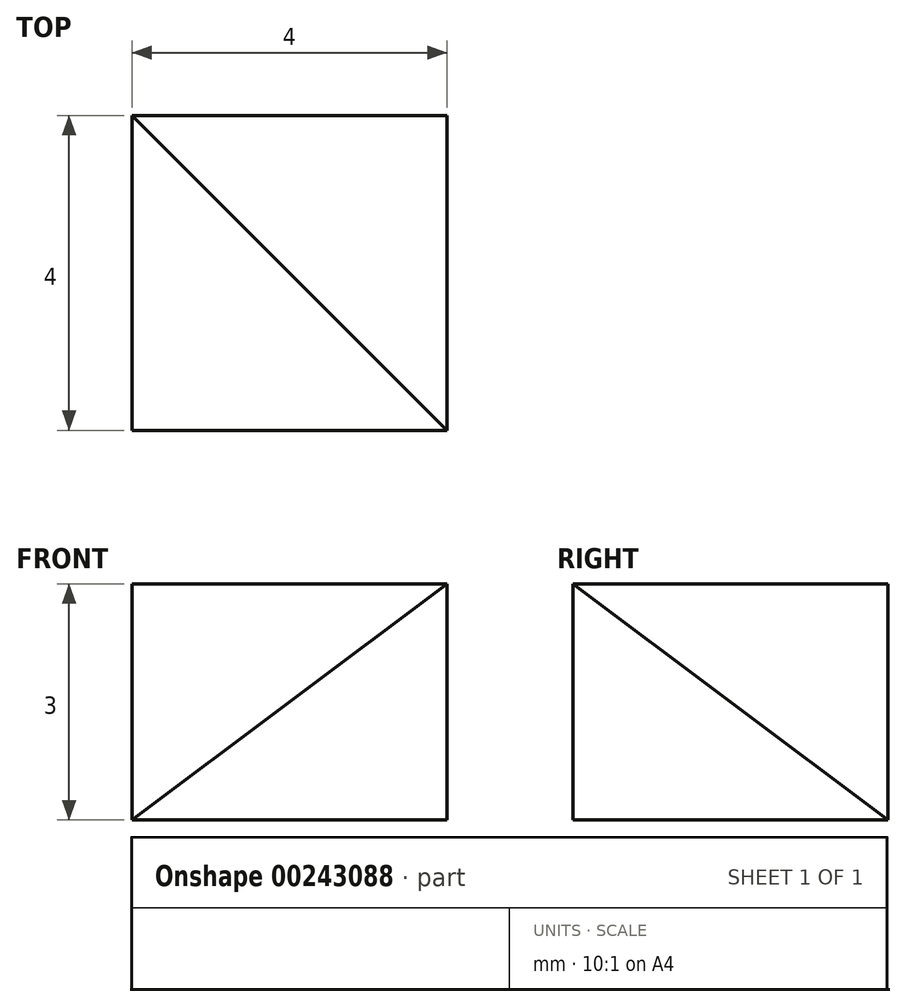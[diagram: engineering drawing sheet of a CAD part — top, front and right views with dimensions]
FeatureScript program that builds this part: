
annotation { "Feature Type Name" : "Feature", "Feature Type Description" : "" }
export const myFeature = defineFeature(function(context is Context, id is Id, definition is map)
    precondition{}
    {
        {
            var Q0;
            Q0=qCreatedBy(makeId("Top.planeOp"),FACE);
            var sketch = newSketch(context, id + "F0", { "sketchPlane" : qUnion([Q0])});
            skLineSegment(sketch, "E0.bottom", {"start": v(0, 0) * mm, "end": v(4, 0) * mm});
            skLineSegment(sketch, "E0.top", {"start": v(0, 4) * mm, "end": v(4, 4) * mm});
            skLineSegment(sketch, "E0.left", {"start": v(0, 0) * mm, "end": v(0, 4) * mm});
            skLineSegment(sketch, "E0.right", {"start": v(4, 0) * mm, "end": v(4, 4) * mm});
            skSolve(sketch);
        }
        {
            var Q0;
            Q0 = qSketchRegion(id + "F0", true);
            extrude(context, id + "F1", {"entities" : qUnion([Q0]), "depth" : 3 * mm});
        }
        {
            var Q0;
            Q0=makeQuery(id+"F1.opExtrude","CAP_VERTEX",VERTEX,{"disambiguationData":[OSD([sQuery(id+"F0.wireOp",EDGE,"E0.top"),sQuery(id+"F0.wireOp",EDGE,"E0.left")])],"isStart":false});
            var Q1;
            Q1=makeQuery(id+"F1.opExtrude","CAP_VERTEX",VERTEX,{"disambiguationData":[OSD([sQuery(id+"F0.wireOp",EDGE,"E0.bottom"),sQuery(id+"F0.wireOp",EDGE,"E0.right")])],"isStart":false});
            var Q2;
            Q2=qCreatedBy(makeId("Origin.pointOp"),VERTEX);
            cPlane(context, id + "F2", {"entities" : qUnion([Q0, Q1, Q2]), "cplaneType" : CPlaneType.THREE_POINT, "offset" : 25 * mm, "width" : 150 * mm, "height" : 150 * mm});
        }
        {
            var Q0;
            Q0=qCreatedBy(id+"F2.planeOp",FACE);
            var sketch = newSketch(context, id + "F3", { "sketchPlane" : qUnion([Q0])});
            skPoint(sketch, "E1.0", {"position": v(0, 5) * mm});
            skPoint(sketch, "E1.1", {"position": v(0, 0) * mm});
            skPoint(sketch, "E1.2", {"position": v(4.66, 1.8) * mm});
            skLineSegment(sketch, "E2", {"start": v(0, 5) * mm, "end": v(4.66, 1.8) * mm});
            skLineSegment(sketch, "E3", {"start": v(0, 0) * mm, "end": v(0, 5) * mm});
            skLineSegment(sketch, "E4", {"start": v(4.66, 1.8) * mm, "end": v(0, 0) * mm});
            skSolve(sketch);
        }
        {
            var Q0;
            Q0 = qSketchRegion(id + "F3", true);
            extrude(context, id + "F4", {"entities" : qUnion([Q0]), "operationType" : NewBodyOperationType.REMOVE, "depth" : 25 * mm});
        }
        {
            var Q0;
            Q0=makeQuery(id+"F4.boolean.opBoolean","MERGE",VERTEX,{"derivedFrom":[makeQuery(id+"F1.opExtrude","CAP_VERTEX",VERTEX,{"disambiguationData":[OSD([sQuery(id+"F0.wireOp",EDGE,"E0.top"),sQuery(id+"F0.wireOp",EDGE,"E0.left")])],"isStart":false}),makeQuery(id+"F4.opExtrude","CAP_VERTEX",VERTEX,{"disambiguationData":[OSD([sQuery(id+"F3.wireOp",EDGE,"E2"),sQuery(id+"F3.wireOp",EDGE,"E3")])],"isStart":true})]});
            var Q1;
            Q1=makeQuery(id+"F4.boolean.opBoolean","MERGE",VERTEX,{"derivedFrom":[makeQuery(id+"F1.opExtrude","CAP_VERTEX",VERTEX,{"disambiguationData":[OSD([sQuery(id+"F0.wireOp",EDGE,"E0.bottom"),sQuery(id+"F0.wireOp",EDGE,"E0.right")])],"isStart":false}),makeQuery(id+"F4.opExtrude","CAP_VERTEX",VERTEX,{"disambiguationData":[OSD([sQuery(id+"F3.wireOp",EDGE,"E2"),sQuery(id+"F3.wireOp",EDGE,"E4")])],"isStart":true})]});
            var Q2;
            Q2=makeQuery(id+"F1.opExtrude","CAP_VERTEX",VERTEX,{"disambiguationData":[OSD([sQuery(id+"F0.wireOp",EDGE,"E0.top"),sQuery(id+"F0.wireOp",EDGE,"E0.right")])],"isStart":true});
            cPlane(context, id + "F5", {"entities" : qUnion([Q0, Q1, Q2]), "cplaneType" : CPlaneType.THREE_POINT, "offset" : 25 * mm, "width" : 150 * mm, "height" : 150 * mm});
        }
        {
            var Q0;
            Q0=qCreatedBy(id+"F5.planeOp",FACE);
            var sketch = newSketch(context, id + "F6", { "sketchPlane" : qUnion([Q0])});
            skPoint(sketch, "E5.0", {"position": v(-2.47, -1.4) * mm});
            skPoint(sketch, "E5.1", {"position": v(2.2, 1.8) * mm});
            skPoint(sketch, "E5.2", {"position": v(2.2, -3.2) * mm});
            skLineSegment(sketch, "E6", {"start": v(-2.47, -1.4) * mm, "end": v(2.2, 1.8) * mm});
            skLineSegment(sketch, "E7", {"start": v(2.2, -3.2) * mm, "end": v(2.2, 1.8) * mm});
            skLineSegment(sketch, "E8", {"start": v(2.2, -3.2) * mm, "end": v(-2.47, -1.4) * mm});
            skSolve(sketch);
        }
        {
            var Q0;
            Q0 = qSketchRegion(id + "F6", true);
            extrude(context, id + "F7", {"entities" : qUnion([Q0]), "operationType" : NewBodyOperationType.REMOVE, "oppositeDirection" : true, "depth" : 25 * mm});
        }
    });
